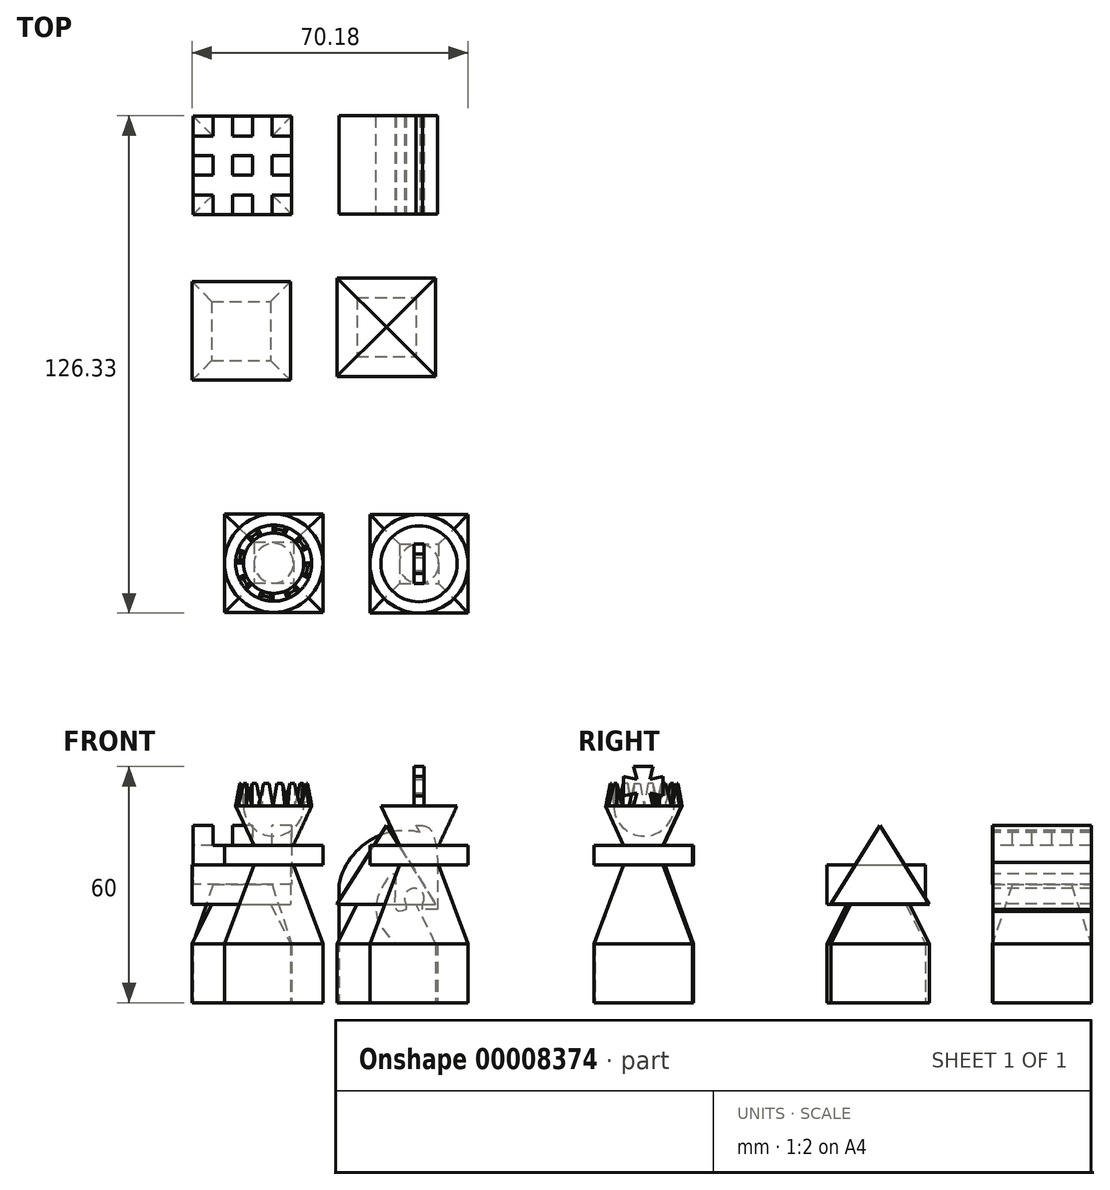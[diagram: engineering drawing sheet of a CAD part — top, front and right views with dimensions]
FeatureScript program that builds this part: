
annotation { "Feature Type Name" : "Feature", "Feature Type Description" : "" }
export const myFeature = defineFeature(function(context is Context, id is Id, definition is map)
    precondition{}
    {
        {
            var Q0;
            Q0=qCreatedBy(makeId("Top.planeOp"),FACE);
            var sketch = newSketch(context, id + "F0", { "sketchPlane" : qUnion([Q0])});
            skLineSegment(sketch, "E0.rect.bottom", {"start": v(-51.31, 37.4) * mm, "end": v(-76.31, 37.4) * mm});
            skLineSegment(sketch, "E0.rect.top", {"start": v(-51.31, 62.4) * mm, "end": v(-76.31, 62.4) * mm});
            skLineSegment(sketch, "E0.rect.left", {"start": v(-51.31, 37.4) * mm, "end": v(-51.31, 62.4) * mm});
            skLineSegment(sketch, "E0.rect.right", {"start": v(-76.31, 37.4) * mm, "end": v(-76.31, 62.4) * mm});
            skPoint(sketch, "E0.rect.middle", {"position": v(-63.81, 49.9) * mm});
            skSolve(sketch);
        }
        {
            var Q0;
            Q0=makeQuery(id+"F0.imprint","IMPRINT",FACE,{"disambiguationData":[TD([[makeQuery(id+"F0.imprint","IMPRINT",EDGE,{"derivedFrom":sQuery(id+"F0.wireOp",EDGE,"E0.rect.bottom")}),-1.0]])]});
            extrude(context, id + "F1", {"entities" : qUnion([Q0]), "depth" : 30 * mm, "hasSecondDirection" : true, "secondDirectionOppositeDirection" : true, "secondDirectionDepth" : 15 * mm});
        }
        {
            var Q0;
            Q0=makeQuery(id+"F1.opExtrude","SWEPT_FACE",FACE,{"disambiguationData":[OSD([sQuery(id+"F0.wireOp",EDGE,"E0.rect.top")])]});
            var sketch = newSketch(context, id + "F2", { "sketchPlane" : qUnion([Q0])});
            skLineSegment(sketch, "E1", {"start": v(51.31, -15) * mm, "end": v(76.31, -15) * mm});
            skLineSegment(sketch, "E2", {"start": v(51.31, 15) * mm, "end": v(56.31, 15) * mm});
            skLineSegment(sketch, "E3", {"start": v(56.31, 15) * mm, "end": v(51.31, 0) * mm});
            skLineSegment(sketch, "E4", {"start": v(76.31, 15) * mm, "end": v(71.31, 15) * mm});
            skLineSegment(sketch, "E5", {"start": v(71.31, 15) * mm, "end": v(76.31, 0) * mm});
            skLineSegment(sketch, "E6", {"start": v(51.31, 15) * mm, "end": v(51.31, 0) * mm});
            skLineSegment(sketch, "E7", {"start": v(76.31, 15) * mm, "end": v(76.31, 0) * mm});
            skSolve(sketch);
        }
        {
            var Q0;
            Q0 = qSketchRegion(id + "F2", true);
            extrude(context, id + "F3", {"entities" : qUnion([Q0]), "operationType" : NewBodyOperationType.REMOVE, "oppositeDirection" : true, "depth" : 25 * mm});
        }
        {
            var Q0;
            {var subQ0=sQuery(id+"F0.wireOp",EDGE,"E0.rect.left");Q0=makeQuery(id+"F3.boolean.opBoolean","SPLIT",FACE,{"disambiguationData":[TD([makeQuery(id+"F3.opExtrude","SWEPT_FACE",FACE,{"disambiguationData":[OSD([sQuery(id+"F2.wireOp",EDGE,"E2")])]})])],"derivedFrom":makeQuery(id+"F1.opExtrude","SWEPT_FACE",FACE,{"disambiguationData":[OSD([subQ0])]})});}
            var sketch = newSketch(context, id + "F4", { "sketchPlane" : qUnion([Q0])});
            skLineSegment(sketch, "E8", {"start": v(37.4, 15) * mm, "end": v(42.4, 15) * mm});
            skLineSegment(sketch, "E9", {"start": v(42.4, 15) * mm, "end": v(37.4, 0) * mm});
            skLineSegment(sketch, "E10", {"start": v(37.4, 0) * mm, "end": v(37.4, 15) * mm});
            skLineSegment(sketch, "E11", {"start": v(62.4, 15) * mm, "end": v(57.4, 15) * mm});
            skLineSegment(sketch, "E12", {"start": v(57.4, 15) * mm, "end": v(62.4, 0) * mm});
            skLineSegment(sketch, "E13", {"start": v(62.4, 0) * mm, "end": v(62.4, 15) * mm});
            skSolve(sketch);
        }
        {
            var Q0;
            Q0=makeQuery(id+"F4.imprint","IMPRINT",FACE,{"disambiguationData":[TD([[makeQuery(id+"F4.imprint","IMPRINT",EDGE,{"derivedFrom":sQuery(id+"F4.wireOp",EDGE,"E8")}),-1.0]])]});
            var Q1;
            Q1=makeQuery(id+"F4.imprint","IMPRINT",FACE,{"disambiguationData":[TD([[makeQuery(id+"F4.imprint","IMPRINT",EDGE,{"derivedFrom":sQuery(id+"F4.wireOp",EDGE,"E11")}),-1.0]])]});
            extrude(context, id + "F5", {"entities" : qUnion([Q0, Q1]), "operationType" : NewBodyOperationType.REMOVE, "oppositeDirection" : true, "depth" : 25 * mm});
        }
        {
            var Q0;
            {var subQ0=sQuery(id+"F0.wireOp",EDGE,"E0.rect.bottom");Q0=makeQuery(id+"F5.boolean.opBoolean","SPLIT",FACE,{"disambiguationData":[TD([makeQuery(id+"F3.boolean.opBoolean","COPY",FACE,{"derivedFrom":makeQuery(id+"F3.opExtrude","SWEPT_FACE",FACE,{"disambiguationData":[OSD([sQuery(id+"F2.wireOp",EDGE,"E2")])]})})])],"derivedFrom":makeQuery(id+"F1.opExtrude","SWEPT_FACE",FACE,{"disambiguationData":[OSD([subQ0])]})});}
            var sketch = newSketch(context, id + "F6", { "sketchPlane" : qUnion([Q0])});
            skLineSegment(sketch, "E14", {"start": v(-71.31, 30) * mm, "end": v(-71.31, 25) * mm});
            skLineSegment(sketch, "E15", {"start": v(-71.31, 25) * mm, "end": v(-66.31, 25) * mm});
            skLineSegment(sketch, "E16", {"start": v(-66.31, 30) * mm, "end": v(-66.31, 25) * mm});
            skLineSegment(sketch, "E17", {"start": v(-61.31, 30) * mm, "end": v(-61.31, 25) * mm});
            skLineSegment(sketch, "E18", {"start": v(-56.31, 30) * mm, "end": v(-56.31, 25) * mm});
            skLineSegment(sketch, "E19.trimOffspring", {"start": v(-61.31, 25) * mm, "end": v(-56.31, 25) * mm});
            skPoint(sketch, "E20.end.orphan", {"position": v(-66.31, 28.3) * mm});
            skPoint(sketch, "E21.start.orphan", {"position": v(-61.31, 28.3) * mm});
            skPoint(sketch, "E22.start.orphan", {"position": v(-56.31, 28.3) * mm});
            skSolve(sketch);
        }
        {
            var Q0;
            {var subQ2=sQuery(id+"F6.wireOp",EDGE,"E14");Q0=makeQuery(id+"F6.imprint","IMPRINT",FACE,{"disambiguationData":[TD([[makeQuery(id+"F6.imprint","IMPRINT",EDGE,{"derivedFrom":subQ2}),1.0]])]});}
            var Q1;
            {var subQ2=sQuery(id+"F6.wireOp",EDGE,"E17");Q1=makeQuery(id+"F6.imprint","IMPRINT",FACE,{"disambiguationData":[TD([[makeQuery(id+"F6.imprint","IMPRINT",EDGE,{"derivedFrom":subQ2}),1.0]])]});}
            extrude(context, id + "F7", {"entities" : qUnion([Q0, Q1]), "operationType" : NewBodyOperationType.REMOVE, "oppositeDirection" : true, "depth" : 25 * mm});
        }
        {
            var Q0;
            {var subQ0=sQuery(id+"F0.wireOp",EDGE,"E0.rect.right");Q0=makeQuery(id+"F3.boolean.opBoolean","SPLIT",FACE,{"disambiguationData":[TD([makeQuery(id+"F3.opExtrude","SWEPT_FACE",FACE,{"disambiguationData":[OSD([sQuery(id+"F2.wireOp",EDGE,"E4")])]})])],"derivedFrom":makeQuery(id+"F1.opExtrude","SWEPT_FACE",FACE,{"disambiguationData":[OSD([subQ0])]})});}
            var sketch = newSketch(context, id + "F8", { "sketchPlane" : qUnion([Q0])});
            skLineSegment(sketch, "E23", {"start": v(-57.4, 25) * mm, "end": v(-52.4, 25) * mm});
            skLineSegment(sketch, "E24", {"start": v(-47.4, 25) * mm, "end": v(-42.4, 25) * mm});
            skLineSegment(sketch, "E25", {"start": v(-57.4, 25) * mm, "end": v(-57.4, 30) * mm});
            skLineSegment(sketch, "E26", {"start": v(-52.4, 25) * mm, "end": v(-52.4, 30) * mm});
            skLineSegment(sketch, "E27", {"start": v(-47.4, 25) * mm, "end": v(-47.4, 30) * mm});
            skLineSegment(sketch, "E28", {"start": v(-42.4, 25) * mm, "end": v(-42.4, 30) * mm});
            skSolve(sketch);
        }
        {
            var Q0;
            Q0=makeQuery(id+"F8.imprint","IMPRINT",FACE,{"disambiguationData":[TD([[makeQuery(id+"F8.imprint","IMPRINT",EDGE,{"derivedFrom":sQuery(id+"F8.wireOp",EDGE,"E23")}),1.0]])]});
            var Q1;
            Q1=makeQuery(id+"F8.imprint","IMPRINT",FACE,{"disambiguationData":[TD([[makeQuery(id+"F8.imprint","IMPRINT",EDGE,{"derivedFrom":sQuery(id+"F8.wireOp",EDGE,"E24")}),1.0]])]});
            extrude(context, id + "F9", {"entities" : qUnion([Q0, Q1]), "operationType" : NewBodyOperationType.REMOVE, "oppositeDirection" : true, "depth" : 25 * mm});
        }
        {
            var Q0;
            Q0=qCreatedBy(makeId("Top.planeOp"),FACE);
            var sketch = newSketch(context, id + "F10", { "sketchPlane" : qUnion([Q0])});
            skLineSegment(sketch, "E29.bottom", {"start": v(-76.64, -4.67) * mm, "end": v(-51.64, -4.67) * mm});
            skLineSegment(sketch, "E29.top", {"start": v(-76.64, 20.33) * mm, "end": v(-51.64, 20.33) * mm});
            skLineSegment(sketch, "E29.left", {"start": v(-76.64, -4.67) * mm, "end": v(-76.64, 20.33) * mm});
            skLineSegment(sketch, "E29.right", {"start": v(-51.64, -4.67) * mm, "end": v(-51.64, 20.33) * mm});
            skSolve(sketch);
        }
        {
            var Q0;
            Q0=makeQuery(id+"F10.imprint","IMPRINT",FACE,{"disambiguationData":[TD([[makeQuery(id+"F10.imprint","IMPRINT",EDGE,{"derivedFrom":sQuery(id+"F10.wireOp",EDGE,"E29.bottom")}),1.0]])]});
            extrude(context, id + "F11", {"entities" : qUnion([Q0]), "depth" : 20 * mm, "hasSecondDirection" : true, "secondDirectionOppositeDirection" : true, "secondDirectionDepth" : 15 * mm});
        }
        {
            var Q0;
            Q0=makeQuery(id+"F11.opExtrude","SWEPT_FACE",FACE,{"disambiguationData":[OSD([sQuery(id+"F10.wireOp",EDGE,"E29.right")])]});
            var sketch = newSketch(context, id + "F12", { "sketchPlane" : qUnion([Q0])});
            skLineSegment(sketch, "E30", {"start": v(-4.67, 0) * mm, "end": v(-4.67, 10) * mm});
            skLineSegment(sketch, "E31", {"start": v(-4.67, 10) * mm, "end": v(0.33, 10) * mm});
            skLineSegment(sketch, "E32", {"start": v(0.33, 10) * mm, "end": v(-4.67, 0) * mm});
            skLineSegment(sketch, "E33", {"start": v(20.33, 10) * mm, "end": v(15.33, 10) * mm});
            skLineSegment(sketch, "E34", {"start": v(15.33, 10) * mm, "end": v(20.33, 0) * mm});
            skLineSegment(sketch, "E35", {"start": v(20.33, 0) * mm, "end": v(20.33, 10) * mm});
            skSolve(sketch);
        }
        {
            var Q0;
            Q0=makeQuery(id+"F12.imprint","IMPRINT",FACE,{"disambiguationData":[TD([[makeQuery(id+"F12.imprint","IMPRINT",EDGE,{"derivedFrom":sQuery(id+"F12.wireOp",EDGE,"E30")}),1.0]])]});
            var Q1;
            Q1=makeQuery(id+"F12.imprint","IMPRINT",FACE,{"disambiguationData":[TD([[makeQuery(id+"F12.imprint","IMPRINT",EDGE,{"derivedFrom":sQuery(id+"F12.wireOp",EDGE,"E33")}),1.0]])]});
            extrude(context, id + "F13", {"entities" : qUnion([Q0, Q1]), "operationType" : NewBodyOperationType.REMOVE, "oppositeDirection" : true, "depth" : 25 * mm});
        }
        {
            var Q0;
            {var subQ0=sQuery(id+"F10.wireOp",EDGE,"E29.bottom");Q0=makeQuery(id+"F13.boolean.opBoolean","SPLIT",FACE,{"disambiguationData":[TD([makeQuery(id+"F13.opExtrude","SWEPT_FACE",FACE,{"disambiguationData":[OSD([sQuery(id+"F12.wireOp",EDGE,"E31")])]})])],"derivedFrom":makeQuery(id+"F11.opExtrude","SWEPT_FACE",FACE,{"disambiguationData":[OSD([subQ0])]})});}
            var sketch = newSketch(context, id + "F14", { "sketchPlane" : qUnion([Q0])});
            skLineSegment(sketch, "E36", {"start": v(-76.64, 0) * mm, "end": v(-76.64, 10) * mm});
            skLineSegment(sketch, "E37", {"start": v(-76.64, 10) * mm, "end": v(-71.64, 10) * mm});
            skLineSegment(sketch, "E38", {"start": v(-71.64, 10) * mm, "end": v(-76.64, 0) * mm});
            skLineSegment(sketch, "E39", {"start": v(-51.64, 10) * mm, "end": v(-56.64, 10) * mm});
            skLineSegment(sketch, "E40", {"start": v(-56.64, 10) * mm, "end": v(-51.64, 0) * mm});
            skLineSegment(sketch, "E41", {"start": v(-51.64, 0) * mm, "end": v(-51.64, 10) * mm});
            skSolve(sketch);
        }
        {
            var Q0;
            Q0=makeQuery(id+"F14.imprint","IMPRINT",FACE,{"disambiguationData":[TD([[makeQuery(id+"F14.imprint","IMPRINT",EDGE,{"derivedFrom":sQuery(id+"F14.wireOp",EDGE,"E36")}),-1.0]])]});
            var Q1;
            Q1=makeQuery(id+"F14.imprint","IMPRINT",FACE,{"disambiguationData":[TD([[makeQuery(id+"F14.imprint","IMPRINT",EDGE,{"derivedFrom":sQuery(id+"F14.wireOp",EDGE,"E39")}),-1.0]])]});
            extrude(context, id + "F15", {"entities" : qUnion([Q0, Q1]), "operationType" : NewBodyOperationType.REMOVE, "oppositeDirection" : true, "depth" : 25 * mm});
        }
        {
            var Q0;
            Q0=qCreatedBy(makeId("Top.planeOp"),FACE);
            var sketch = newSketch(context, id + "F16", { "sketchPlane" : qUnion([Q0])});
            skLineSegment(sketch, "E42.bottom", {"start": v(-39.28, 62.5) * mm, "end": v(-14.28, 62.5) * mm});
            skLineSegment(sketch, "E42.top", {"start": v(-39.28, 37.5) * mm, "end": v(-14.28, 37.5) * mm});
            skLineSegment(sketch, "E42.left", {"start": v(-39.28, 62.5) * mm, "end": v(-39.28, 37.5) * mm});
            skLineSegment(sketch, "E42.right", {"start": v(-14.28, 62.5) * mm, "end": v(-14.28, 37.5) * mm});
            skSolve(sketch);
        }
        {
            var Q0;
            Q0=makeQuery(id+"F16.imprint","IMPRINT",FACE,{"disambiguationData":[TD([[makeQuery(id+"F16.imprint","IMPRINT",EDGE,{"derivedFrom":sQuery(id+"F16.wireOp",EDGE,"E42.bottom")}),-1.0]])]});
            extrude(context, id + "F17", {"entities" : qUnion([Q0]), "depth" : 30 * mm, "hasSecondDirection" : true, "secondDirectionOppositeDirection" : true, "secondDirectionDepth" : 15 * mm});
        }
        {
            var Q0;
            Q0=makeQuery(id+"F17.opExtrude","SWEPT_FACE",FACE,{"disambiguationData":[OSD([sQuery(id+"F16.wireOp",EDGE,"E42.top")])]});
            var sketch = newSketch(context, id + "F18", { "sketchPlane" : qUnion([Q0])});
            skLineSegment(sketch, "E43", {"start": v(-39.28, 0) * mm, "end": v(-39.28, 15) * mm});
            skArc(sketch, "E44", {"start": v(-18.7, 28.27) * mm, "mid": v(-31.8, 26) * mm, "end": v(-39.28, 15) * mm});
            skLineSegment(sketch, "E45", {"start": v(-18.7, 28.27) * mm, "end": v(-19.7, 30) * mm});
            skFitSpline(sketch, "E46", {"points": [v(-19.7, 30) * mm, v(-16.08, 29.03) * mm, v(-14.28, 8.72) * mm], "startDerivative": vector(13.5, 0.62) * mm, "endDerivative": vector(-0.75, -38.03) * mm});
            skLineSegment(sketch, "E47", {"start": v(-14.28, 8.72) * mm, "end": v(-18.1, 8.72) * mm});
            skLineSegment(sketch, "E48", {"start": v(-18.1, 8.72) * mm, "end": v(-18.1, 10.15) * mm});
            skArc(sketch, "E49", {"start": v(-18.1, 10.15) * mm, "mid": v(-20.17, 14.03) * mm, "end": v(-22.23, 10.15) * mm});
            skLineSegment(sketch, "E50", {"start": v(-22.23, 10.15) * mm, "end": v(-22.23, 8.72) * mm});
            skFitSpline(sketch, "E51", {"points": [v(-22.23, 8.72) * mm, v(-24.76, 8.72) * mm, v(-25.18, 17.57) * mm, v(-29.9, 9.99) * mm, v(-25.01, 0) * mm], "startDerivative": vector(-21.5, -9.14) * mm, "endDerivative": vector(26.9, -28.6) * mm});
            skLineSegment(sketch, "E52", {"start": v(-39.28, 0) * mm, "end": v(-14.28, 0) * mm});
            skLineSegment(sketch, "E53", {"start": v(-14.28, 0) * mm, "end": v(-14.28, 30) * mm});
            skLineSegment(sketch, "E54", {"start": v(-14.28, 30) * mm, "end": v(-39.28, 30) * mm});
            skLineSegment(sketch, "E55", {"start": v(-39.28, 30) * mm, "end": v(-39.28, 0) * mm});
            skSolve(sketch);
        }
        {
            var Q0;
            Q0=makeQuery(id+"F18.imprint","IMPRINT",FACE,{"disambiguationData":[TD([[makeQuery(id+"F18.imprint","IMPRINT",EDGE,{"derivedFrom":sQuery(id+"F18.wireOp",EDGE,"E44")}),-1.0]])]});
            var Q1;
            {var subQ0=sQuery(id+"F18.wireOp",EDGE,"E54");var subQ1=sQuery(id+"F18.wireOp",EDGE,"E46");var subQ2=makeQuery(id+"F18.imprint","INTERSECT",VERTEX,{"derivedFrom":[subQ1,subQ0]});Q1=makeQuery(id+"F18.imprint","IMPRINT",FACE,{"disambiguationData":[TD([[makeQuery(id+"F18.imprint","IMPRINT",EDGE,{"disambiguationData":[TD([[subQ2,-1.0]])],"derivedFrom":subQ1}),1.0]])]});}
            var Q2;
            {var subQ0=sQuery(id+"F18.wireOp",EDGE,"E47");Q2=makeQuery(id+"F18.imprint","IMPRINT",FACE,{"disambiguationData":[TD([[makeQuery(id+"F18.imprint","IMPRINT",EDGE,{"derivedFrom":subQ0}),1.0]])]});}
            extrude(context, id + "F19", {"entities" : qUnion([Q0, Q1, Q2]), "operationType" : NewBodyOperationType.REMOVE, "oppositeDirection" : true, "depth" : 25 * mm});
        }
        {
            var Q0;
            Q0=qCreatedBy(makeId("Top.planeOp"),FACE);
            var sketch = newSketch(context, id + "F20", { "sketchPlane" : qUnion([Q0])});
            skLineSegment(sketch, "E56.bottom", {"start": v(-39.73, 21.33) * mm, "end": v(-14.73, 21.33) * mm});
            skLineSegment(sketch, "E56.top", {"start": v(-39.73, -3.67) * mm, "end": v(-14.73, -3.67) * mm});
            skLineSegment(sketch, "E56.left", {"start": v(-39.73, 21.33) * mm, "end": v(-39.73, -3.67) * mm});
            skLineSegment(sketch, "E56.right", {"start": v(-14.73, 21.33) * mm, "end": v(-14.73, -3.67) * mm});
            skSolve(sketch);
        }
        {
            var Q0;
            Q0=makeQuery(id+"F20.imprint","IMPRINT",FACE,{"disambiguationData":[TD([[makeQuery(id+"F20.imprint","IMPRINT",EDGE,{"derivedFrom":sQuery(id+"F20.wireOp",EDGE,"E56.bottom")}),-1.0]])]});
            extrude(context, id + "F21", {"entities" : qUnion([Q0]), "depth" : 30 * mm, "hasSecondDirection" : true, "secondDirectionOppositeDirection" : true, "secondDirectionDepth" : 15 * mm});
        }
        {
            var Q0;
            Q0=makeQuery(id+"F21.opExtrude","SWEPT_FACE",FACE,{"disambiguationData":[OSD([sQuery(id+"F20.wireOp",EDGE,"E56.right")])]});
            var sketch = newSketch(context, id + "F22", { "sketchPlane" : qUnion([Q0])});
            skLineSegment(sketch, "E57", {"start": v(-3.67, 0) * mm, "end": v(-3.67, 10) * mm});
            skLineSegment(sketch, "E58", {"start": v(-3.67, 10) * mm, "end": v(1.33, 10) * mm});
            skLineSegment(sketch, "E59", {"start": v(1.33, 10) * mm, "end": v(-3.67, 0) * mm});
            skLineSegment(sketch, "E60", {"start": v(16.33, 10) * mm, "end": v(21.33, 10) * mm});
            skLineSegment(sketch, "E61", {"start": v(21.33, 10) * mm, "end": v(21.33, 0) * mm});
            skLineSegment(sketch, "E62", {"start": v(21.33, 0) * mm, "end": v(16.33, 10) * mm});
            skSolve(sketch);
        }
        {
            var Q0;
            Q0=makeQuery(id+"F22.imprint","IMPRINT",FACE,{"disambiguationData":[TD([[makeQuery(id+"F22.imprint","IMPRINT",EDGE,{"derivedFrom":sQuery(id+"F22.wireOp",EDGE,"E57")}),1.0]])]});
            var Q1;
            Q1=makeQuery(id+"F22.imprint","IMPRINT",FACE,{"disambiguationData":[TD([[makeQuery(id+"F22.imprint","IMPRINT",EDGE,{"derivedFrom":sQuery(id+"F22.wireOp",EDGE,"E60")}),-1.0]])]});
            extrude(context, id + "F23", {"entities" : qUnion([Q0, Q1]), "operationType" : NewBodyOperationType.REMOVE, "oppositeDirection" : true, "depth" : 25 * mm});
        }
        {
            var Q0;
            {var subQ0=sQuery(id+"F20.wireOp",EDGE,"E56.top");Q0=makeQuery(id+"F23.boolean.opBoolean","SPLIT",FACE,{"disambiguationData":[TD([makeQuery(id+"F23.opExtrude","SWEPT_FACE",FACE,{"disambiguationData":[OSD([sQuery(id+"F22.wireOp",EDGE,"E58")])]})])],"derivedFrom":makeQuery(id+"F21.opExtrude","SWEPT_FACE",FACE,{"disambiguationData":[OSD([subQ0])]})});}
            var sketch = newSketch(context, id + "F24", { "sketchPlane" : qUnion([Q0])});
            skLineSegment(sketch, "E63", {"start": v(-39.73, 10) * mm, "end": v(-39.73, 0) * mm});
            skLineSegment(sketch, "E64", {"start": v(-39.73, 0) * mm, "end": v(-34.73, 10) * mm});
            skLineSegment(sketch, "E65", {"start": v(-34.73, 10) * mm, "end": v(-39.73, 10) * mm});
            skLineSegment(sketch, "E66", {"start": v(-14.73, 10) * mm, "end": v(-19.73, 10) * mm});
            skLineSegment(sketch, "E67", {"start": v(-19.73, 10) * mm, "end": v(-14.73, 0) * mm});
            skLineSegment(sketch, "E68", {"start": v(-14.73, 0) * mm, "end": v(-14.73, 10) * mm});
            skSolve(sketch);
        }
        {
            var Q0;
            Q0=makeQuery(id+"F24.imprint","IMPRINT",FACE,{"disambiguationData":[TD([[makeQuery(id+"F24.imprint","IMPRINT",EDGE,{"derivedFrom":sQuery(id+"F24.wireOp",EDGE,"E63")}),1.0]])]});
            var Q1;
            Q1=makeQuery(id+"F24.imprint","IMPRINT",FACE,{"disambiguationData":[TD([[makeQuery(id+"F24.imprint","IMPRINT",EDGE,{"derivedFrom":sQuery(id+"F24.wireOp",EDGE,"E66")}),-1.0]])]});
            extrude(context, id + "F25", {"entities" : qUnion([Q0, Q1]), "operationType" : NewBodyOperationType.REMOVE, "oppositeDirection" : true, "depth" : 25 * mm});
        }
        {
            var Q0;
            {var subQ0=sQuery(id+"F20.wireOp",EDGE,"E56.right");Q0=makeQuery(id+"F25.boolean.opBoolean","SPLIT",FACE,{"disambiguationData":[TD([makeQuery(id+"F23.boolean.opBoolean","COPY",FACE,{"derivedFrom":makeQuery(id+"F23.opExtrude","SWEPT_FACE",FACE,{"disambiguationData":[OSD([sQuery(id+"F22.wireOp",EDGE,"E58")])]})})])],"derivedFrom":makeQuery(id+"F21.opExtrude","SWEPT_FACE",FACE,{"disambiguationData":[OSD([subQ0])]})});}
            var sketch = newSketch(context, id + "F26", { "sketchPlane" : qUnion([Q0])});
            skLineSegment(sketch, "E69", {"start": v(-3.67, 30) * mm, "end": v(21.33, 30) * mm});
            skLineSegment(sketch, "E70", {"start": v(8.83, 30) * mm, "end": v(-3.67, 10) * mm});
            skLineSegment(sketch, "E71", {"start": v(-3.67, 10) * mm, "end": v(21.33, 10) * mm});
            skLineSegment(sketch, "E72", {"start": v(21.33, 10) * mm, "end": v(8.83, 30) * mm});
            skSolve(sketch);
        }
        {
            var Q0;
            {var subQ3=sQuery(id+"F26.wireOp",EDGE,"E70");Q0=makeQuery(id+"F26.imprint","IMPRINT",FACE,{"disambiguationData":[TD([[makeQuery(id+"F26.imprint","IMPRINT",EDGE,{"derivedFrom":subQ3}),-1.0]])]});}
            var Q1;
            {var subQ3=sQuery(id+"F26.wireOp",EDGE,"E72");Q1=makeQuery(id+"F26.imprint","IMPRINT",FACE,{"disambiguationData":[TD([[makeQuery(id+"F26.imprint","IMPRINT",EDGE,{"derivedFrom":subQ3}),-1.0]])]});}
            extrude(context, id + "F27", {"entities" : qUnion([Q0, Q1]), "operationType" : NewBodyOperationType.REMOVE, "oppositeDirection" : true, "depth" : 25 * mm});
        }
        {
            var Q0;
            {var subQ0=sQuery(id+"F20.wireOp",EDGE,"E56.top");Q0=makeQuery(id+"F23.boolean.opBoolean","SPLIT",FACE,{"disambiguationData":[TD([makeQuery(id+"F23.opExtrude","SWEPT_FACE",FACE,{"disambiguationData":[OSD([sQuery(id+"F22.wireOp",EDGE,"E59")])]})])],"derivedFrom":makeQuery(id+"F21.opExtrude","SWEPT_FACE",FACE,{"disambiguationData":[OSD([subQ0])]})});}
            var sketch = newSketch(context, id + "F28", { "sketchPlane" : qUnion([Q0])});
            skLineSegment(sketch, "E73", {"start": v(-39.73, 30.07) * mm, "end": v(-39.73, 10.07) * mm});
            skLineSegment(sketch, "E74", {"start": v(-39.73, 10.07) * mm, "end": v(-14.73, 10.07) * mm});
            skLineSegment(sketch, "E75", {"start": v(-14.73, 10.07) * mm, "end": v(-14.73, 30.07) * mm});
            skLineSegment(sketch, "E76", {"start": v(-14.73, 30.07) * mm, "end": v(-39.73, 30.07) * mm});
            skLineSegment(sketch, "E77", {"start": v(-39.73, 10.07) * mm, "end": v(-27.23, 30.07) * mm});
            skLineSegment(sketch, "E78", {"start": v(-27.23, 30.07) * mm, "end": v(-14.73, 10.07) * mm});
            skSolve(sketch);
        }
        {
            var Q0;
            {var subQ2=sQuery(id+"F28.wireOp",EDGE,"E73");Q0=makeQuery(id+"F28.imprint","IMPRINT",FACE,{"disambiguationData":[TD([[makeQuery(id+"F28.imprint","IMPRINT",EDGE,{"derivedFrom":subQ2}),1.0]])]});}
            var Q1;
            {var subQ2=sQuery(id+"F28.wireOp",EDGE,"E75");Q1=makeQuery(id+"F28.imprint","IMPRINT",FACE,{"disambiguationData":[TD([[makeQuery(id+"F28.imprint","IMPRINT",EDGE,{"derivedFrom":subQ2}),1.0]])]});}
            extrude(context, id + "F29", {"entities" : qUnion([Q0, Q1]), "operationType" : NewBodyOperationType.REMOVE, "oppositeDirection" : true, "depth" : 25 * mm});
        }
        {
            var Q0;
            Q0=qCreatedBy(makeId("Top.planeOp"),FACE);
            var sketch = newSketch(context, id + "F30", { "sketchPlane" : qUnion([Q0])});
            skLineSegment(sketch, "E79.bottom", {"start": v(-68.4, -38.66) * mm, "end": v(-43.4, -38.66) * mm});
            skLineSegment(sketch, "E79.top", {"start": v(-68.4, -63.66) * mm, "end": v(-43.4, -63.66) * mm});
            skLineSegment(sketch, "E79.left", {"start": v(-68.4, -38.66) * mm, "end": v(-68.4, -63.66) * mm});
            skLineSegment(sketch, "E79.right", {"start": v(-43.4, -38.66) * mm, "end": v(-43.4, -63.66) * mm});
            skSolve(sketch);
        }
        {
            var Q0;
            Q0=makeQuery(id+"F30.imprint","IMPRINT",FACE,{"disambiguationData":[TD([[makeQuery(id+"F30.imprint","IMPRINT",EDGE,{"derivedFrom":sQuery(id+"F30.wireOp",EDGE,"E79.bottom")}),-1.0]])]});
            extrude(context, id + "F31", {"entities" : qUnion([Q0]), "depth" : 25 * mm, "hasSecondDirection" : true, "secondDirectionOppositeDirection" : true, "secondDirectionDepth" : 15 * mm});
        }
        {
            var Q0;
            Q0=makeQuery(id+"F31.opExtrude","SWEPT_FACE",FACE,{"disambiguationData":[OSD([sQuery(id+"F30.wireOp",EDGE,"E79.right")])]});
            var sketch = newSketch(context, id + "F32", { "sketchPlane" : qUnion([Q0])});
            skLineSegment(sketch, "E80", {"start": v(-63.66, 20) * mm, "end": v(-56.16, 20) * mm});
            skLineSegment(sketch, "E81", {"start": v(-56.16, 20) * mm, "end": v(-63.66, 0) * mm});
            skPoint(sketch, "E82.end.orphan", {"position": v(-64.81, 0) * mm});
            skLineSegment(sketch, "E83.trimOffspring", {"start": v(-38.66, 20) * mm, "end": v(-37.97, 20) * mm});
            skLineSegment(sketch, "E84", {"start": v(-45.82, 20) * mm, "end": v(-38.66, 20) * mm});
            skLineSegment(sketch, "E85", {"start": v(-38.66, 0) * mm, "end": v(-45.82, 20) * mm});
            skSolve(sketch);
        }
        {
            var Q0;
            {var subQ2=sQuery(id+"F32.wireOp",EDGE,"E84");Q0=makeQuery(id+"F32.imprint","IMPRINT",FACE,{"disambiguationData":[TD([[makeQuery(id+"F32.imprint","IMPRINT",EDGE,{"derivedFrom":subQ2}),-1.0]])]});}
            var Q1;
            {var subQ2=sQuery(id+"F32.wireOp",EDGE,"E80");Q1=makeQuery(id+"F32.imprint","IMPRINT",FACE,{"disambiguationData":[TD([[makeQuery(id+"F32.imprint","IMPRINT",EDGE,{"derivedFrom":subQ2}),-1.0]])]});}
            extrude(context, id + "F33", {"entities" : qUnion([Q0, Q1]), "operationType" : NewBodyOperationType.REMOVE, "oppositeDirection" : true, "depth" : 25 * mm});
        }
        {
            var Q0;
            Q0=makeQuery(id+"F31.opExtrude","SWEPT_FACE",FACE,{"disambiguationData":[OSD([sQuery(id+"F30.wireOp",EDGE,"E79.top")])]});
            var sketch = newSketch(context, id + "F34", { "sketchPlane" : qUnion([Q0])});
            skLineSegment(sketch, "E86", {"start": v(-68.4, 20) * mm, "end": v(-60.9, 20) * mm});
            skLineSegment(sketch, "E87", {"start": v(-60.9, 20) * mm, "end": v(-68.4, 0) * mm});
            skLineSegment(sketch, "E88", {"start": v(-50.9, 20) * mm, "end": v(-43.4, 0) * mm});
            skPoint(sketch, "E89.end.orphan", {"position": v(-60.9, 17.43) * mm});
            skPoint(sketch, "E90.orphan", {"position": v(-43.4, 17.43) * mm});
            skLineSegment(sketch, "E91.trimOffspring", {"start": v(-50.9, 20) * mm, "end": v(-43.4, 20) * mm});
            skLineSegment(sketch, "E92", {"start": v(-68.4, 20) * mm, "end": v(-68.4, 0) * mm});
            skLineSegment(sketch, "E93", {"start": v(-43.4, 20) * mm, "end": v(-43.4, 0) * mm});
            skSolve(sketch);
        }
        {
            var Q0;
            Q0=makeQuery(id+"F34.imprint","IMPRINT",FACE,{"disambiguationData":[TD([[makeQuery(id+"F34.imprint","IMPRINT",EDGE,{"derivedFrom":sQuery(id+"F34.wireOp",EDGE,"E86")}),-1.0]])]});
            var Q1;
            Q1=makeQuery(id+"F34.imprint","IMPRINT",FACE,{"disambiguationData":[TD([[makeQuery(id+"F34.imprint","IMPRINT",EDGE,{"derivedFrom":sQuery(id+"F34.wireOp",EDGE,"E88")}),1.0]])]});
            extrude(context, id + "F35", {"entities" : qUnion([Q0, Q1]), "operationType" : NewBodyOperationType.REMOVE, "oppositeDirection" : true, "depth" : 25 * mm});
        }
        {
            var Q0;
            Q0=makeQuery(id+"F31.opExtrude","CAP_FACE",FACE,{"disambiguationData":[OSD([sQuery(id+"F30.wireOp",EDGE,"E79.bottom"),sQuery(id+"F30.wireOp",EDGE,"E79.top"),sQuery(id+"F30.wireOp",EDGE,"E79.left"),sQuery(id+"F30.wireOp",EDGE,"E79.right")])],"isStart":false});
            var sketch = newSketch(context, id + "F36", { "sketchPlane" : qUnion([Q0])});
            skLineSegment(sketch, "E94", {"start": v(-68.4, -38.66) * mm, "end": v(-43.4, -63.66) * mm});
            skCircle(sketch, "E95", {"center": v(-55.9, -51.16) * mm, "radius": 12.5 * mm});
            skSolve(sketch);
        }
        {
            var Q0;
            {var subQ0=sQuery(id+"F36.wireOp",EDGE,"E94");var subQ3=sQuery(id+"F36.wireOp",EDGE,"E95");var subQ4=makeQuery(id+"F36.imprint","INTERSECT",VERTEX,{"disambiguationData":[OD(0.0)],"derivedFrom":[subQ0,subQ3]});Q0=makeQuery(id+"F36.imprint","IMPRINT",FACE,{"disambiguationData":[TD([[makeQuery(id+"F36.imprint","IMPRINT",EDGE,{"disambiguationData":[TD([[subQ4,-1.0]])],"derivedFrom":subQ3}),-1.0]])]});}
            var Q1;
            {var subQ0=sQuery(id+"F36.wireOp",EDGE,"E94");var subQ3=sQuery(id+"F36.wireOp",EDGE,"E95");var subQ4=makeQuery(id+"F36.imprint","INTERSECT",VERTEX,{"disambiguationData":[OD(0.0)],"derivedFrom":[subQ0,subQ3]});Q1=makeQuery(id+"F36.imprint","IMPRINT",FACE,{"disambiguationData":[TD([[makeQuery(id+"F36.imprint","IMPRINT",EDGE,{"disambiguationData":[TD([[subQ4,1.0]])],"derivedFrom":subQ3}),-1.0]])]});}
            var Q2;
            {var subQ0=sQuery(id+"F36.wireOp",EDGE,"E95");var subQ1=makeQuery(id+"F31.opExtrude","CAP_EDGE",EDGE,{"disambiguationData":[OSD([sQuery(id+"F30.wireOp",EDGE,"E79.bottom")])],"isStart":false});var subQ2=makeQuery(id+"F36.imprint","INTERSECT",VERTEX,{"derivedFrom":[subQ1,subQ0]});Q2=makeQuery(id+"F36.imprint","IMPRINT",FACE,{"disambiguationData":[TD([[makeQuery(id+"F36.imprint","IMPRINT",EDGE,{"disambiguationData":[TD([[subQ2,1.0]])],"derivedFrom":subQ0}),-1.0]])]});}
            var Q3;
            {var subQ0=sQuery(id+"F36.wireOp",EDGE,"E94");var subQ3=sQuery(id+"F36.wireOp",EDGE,"E95");var subQ4=makeQuery(id+"F36.imprint","INTERSECT",VERTEX,{"disambiguationData":[OD(1.0)],"derivedFrom":[subQ0,subQ3]});Q3=makeQuery(id+"F36.imprint","IMPRINT",FACE,{"disambiguationData":[TD([[makeQuery(id+"F36.imprint","IMPRINT",EDGE,{"disambiguationData":[TD([[subQ4,-1.0]])],"derivedFrom":subQ3}),-1.0]])]});}
            var Q4;
            {var subQ0=sQuery(id+"F36.wireOp",EDGE,"E95");var subQ1=makeQuery(id+"F31.opExtrude","CAP_EDGE",EDGE,{"disambiguationData":[OSD([sQuery(id+"F30.wireOp",EDGE,"E79.left")])],"isStart":false});var subQ2=makeQuery(id+"F36.imprint","INTERSECT",VERTEX,{"derivedFrom":[subQ1,subQ0]});Q4=makeQuery(id+"F36.imprint","IMPRINT",FACE,{"disambiguationData":[TD([[makeQuery(id+"F36.imprint","IMPRINT",EDGE,{"disambiguationData":[TD([[subQ2,-1.0]])],"derivedFrom":subQ0}),-1.0]])]});}
            var Q5;
            {var subQ0=sQuery(id+"F36.wireOp",EDGE,"E94");var subQ3=sQuery(id+"F36.wireOp",EDGE,"E95");var subQ4=makeQuery(id+"F36.imprint","INTERSECT",VERTEX,{"disambiguationData":[OD(1.0)],"derivedFrom":[subQ0,subQ3]});Q5=makeQuery(id+"F36.imprint","IMPRINT",FACE,{"disambiguationData":[TD([[makeQuery(id+"F36.imprint","IMPRINT",EDGE,{"disambiguationData":[TD([[subQ4,1.0]])],"derivedFrom":subQ3}),-1.0]])]});}
            extrude(context, id + "F37", {"entities" : qUnion([Q0, Q1, Q2, Q3, Q4, Q5]), "operationType" : NewBodyOperationType.REMOVE, "oppositeDirection" : true, "depth" : (5) * mm});
        }
        {
            var Q0;
            Q0=qCreatedBy(makeId("Top.planeOp"),FACE);
            var sketch = newSketch(context, id + "F38", { "sketchPlane" : qUnion([Q0])});
            skLineSegment(sketch, "E96.bottom", {"start": v(-31.46, -38.82) * mm, "end": v(-6.46, -38.82) * mm});
            skLineSegment(sketch, "E96.top", {"start": v(-31.46, -63.82) * mm, "end": v(-6.46, -63.82) * mm});
            skLineSegment(sketch, "E96.left", {"start": v(-31.46, -38.82) * mm, "end": v(-31.46, -63.82) * mm});
            skLineSegment(sketch, "E96.right", {"start": v(-6.46, -38.82) * mm, "end": v(-6.46, -63.82) * mm});
            skSolve(sketch);
        }
        {
            var Q0;
            Q0=makeQuery(id+"F38.imprint","IMPRINT",FACE,{"disambiguationData":[TD([[makeQuery(id+"F38.imprint","IMPRINT",EDGE,{"derivedFrom":sQuery(id+"F38.wireOp",EDGE,"E96.bottom")}),-1.0]])]});
            extrude(context, id + "F39", {"entities" : qUnion([Q0]), "depth" : 25 * mm, "hasSecondDirection" : true, "secondDirectionOppositeDirection" : true, "secondDirectionDepth" : 15 * mm});
        }
        {
            var Q0;
            Q0=makeQuery(id+"F39.opExtrude","SWEPT_FACE",FACE,{"disambiguationData":[OSD([sQuery(id+"F38.wireOp",EDGE,"E96.right")])]});
            var sketch = newSketch(context, id + "F40", { "sketchPlane" : qUnion([Q0])});
            skLineSegment(sketch, "E97", {"start": v(-63.82, 25) * mm, "end": v(-63.82, 0) * mm});
            skLineSegment(sketch, "E98", {"start": v(-63.82, 0) * mm, "end": v(-38.82, 0) * mm});
            skLineSegment(sketch, "E99", {"start": v(-38.82, 0) * mm, "end": v(-38.82, 25) * mm});
            skLineSegment(sketch, "E100", {"start": v(-38.82, 25) * mm, "end": v(-63.82, 25) * mm});
            skLineSegment(sketch, "E101", {"start": v(-63.82, 0) * mm, "end": v(-63.82, 20) * mm});
            skLineSegment(sketch, "E102", {"start": v(-63.82, 20) * mm, "end": v(-56.32, 20) * mm});
            skLineSegment(sketch, "E103", {"start": v(-56.32, 20) * mm, "end": v(-63.82, 0) * mm});
            skLineSegment(sketch, "E104", {"start": v(-38.82, 0) * mm, "end": v(-38.82, 20) * mm});
            skLineSegment(sketch, "E105", {"start": v(-38.82, 20) * mm, "end": v(-46.32, 20) * mm});
            skLineSegment(sketch, "E106", {"start": v(-46.32, 20) * mm, "end": v(-38.82, 0) * mm});
            skLineSegment(sketch, "E107", {"start": v(-38.82, 20) * mm, "end": v(-38.82, 0) * mm});
            skSolve(sketch);
        }
        {
            var Q0;
            {var subQ2=sQuery(id+"F40.wireOp",EDGE,"E102");Q0=makeQuery(id+"F40.imprint","IMPRINT",FACE,{"disambiguationData":[TD([[makeQuery(id+"F40.imprint","IMPRINT",EDGE,{"derivedFrom":subQ2}),-1.0]])]});}
            var Q1;
            {var subQ2=sQuery(id+"F40.wireOp",EDGE,"E105");Q1=makeQuery(id+"F40.imprint","IMPRINT",FACE,{"disambiguationData":[TD([[makeQuery(id+"F40.imprint","IMPRINT",EDGE,{"derivedFrom":subQ2}),1.0]])]});}
            extrude(context, id + "F41", {"entities" : qUnion([Q0, Q1]), "operationType" : NewBodyOperationType.REMOVE, "oppositeDirection" : true, "depth" : 25 * mm});
        }
        {
            var Q0;
            {var subQ2=sQuery(id+"F38.wireOp",EDGE,"E96.top");Q0=makeQuery(id+"F41.boolean.opBoolean","SPLIT",FACE,{"disambiguationData":[TD([makeQuery(id+"F41.opExtrude","SWEPT_FACE",FACE,{"disambiguationData":[OSD([sQuery(id+"F40.wireOp",EDGE,"E103")])]})])],"derivedFrom":makeQuery(id+"F39.opExtrude","SWEPT_FACE",FACE,{"disambiguationData":[OSD([subQ2])]})});}
            var sketch = newSketch(context, id + "F42", { "sketchPlane" : qUnion([Q0])});
            skLineSegment(sketch, "E108", {"start": v(-31.46, 0) * mm, "end": v(-31.46, 20) * mm});
            skLineSegment(sketch, "E109", {"start": v(-31.46, 20) * mm, "end": v(-23.96, 20) * mm});
            skLineSegment(sketch, "E110", {"start": v(-23.96, 20) * mm, "end": v(-31.46, 0) * mm});
            skLineSegment(sketch, "E111", {"start": v(-6.46, 0) * mm, "end": v(-6.46, 20) * mm});
            skLineSegment(sketch, "E112", {"start": v(-6.46, 20) * mm, "end": v(-13.96, 20) * mm});
            skLineSegment(sketch, "E113", {"start": v(-13.96, 20) * mm, "end": v(-6.46, 0) * mm});
            skLineSegment(sketch, "E114.bottom", {"start": v(-31.46, 20) * mm, "end": v(-6.46, 20) * mm});
            skLineSegment(sketch, "E114.top", {"start": v(-31.46, 0) * mm, "end": v(-6.46, 0) * mm});
            skLineSegment(sketch, "E114.left", {"start": v(-31.46, 20) * mm, "end": v(-31.46, 0) * mm});
            skLineSegment(sketch, "E114.right", {"start": v(-6.46, 20) * mm, "end": v(-6.46, 0) * mm});
            skSolve(sketch);
        }
        {
            var Q0;
            Q0=makeQuery(id+"F42.imprint","IMPRINT",FACE,{"disambiguationData":[TD([[makeQuery(id+"F42.imprint","IMPRINT",EDGE,{"derivedFrom":sQuery(id+"F42.wireOp",EDGE,"E108")}),-1.0]])]});
            var Q1;
            Q1=makeQuery(id+"F42.imprint","IMPRINT",FACE,{"disambiguationData":[TD([[makeQuery(id+"F42.imprint","IMPRINT",EDGE,{"derivedFrom":sQuery(id+"F42.wireOp",EDGE,"E111")}),1.0]])]});
            extrude(context, id + "F43", {"entities" : qUnion([Q0, Q1]), "operationType" : NewBodyOperationType.REMOVE, "oppositeDirection" : true, "depth" : 25 * mm});
        }
        {
            var Q0;
            Q0=makeQuery(id+"F39.opExtrude","CAP_FACE",FACE,{"disambiguationData":[OSD([sQuery(id+"F38.wireOp",EDGE,"E96.bottom"),sQuery(id+"F38.wireOp",EDGE,"E96.top"),sQuery(id+"F38.wireOp",EDGE,"E96.left"),sQuery(id+"F38.wireOp",EDGE,"E96.right")])],"isStart":false});
            var sketch = newSketch(context, id + "F44", { "sketchPlane" : qUnion([Q0])});
            skLineSegment(sketch, "E115", {"start": v(-31.46, -38.82) * mm, "end": v(-6.46, -63.82) * mm});
            skCircle(sketch, "E116", {"center": v(-18.96, -51.32) * mm, "radius": 12.5 * mm});
            skSolve(sketch);
        }
        {
            var Q0;
            {var subQ0=sQuery(id+"F44.wireOp",EDGE,"E115");var subQ3=sQuery(id+"F44.wireOp",EDGE,"E116");var subQ4=makeQuery(id+"F44.imprint","INTERSECT",VERTEX,{"disambiguationData":[OD(0.0)],"derivedFrom":[subQ0,subQ3]});Q0=makeQuery(id+"F44.imprint","IMPRINT",FACE,{"disambiguationData":[TD([[makeQuery(id+"F44.imprint","IMPRINT",EDGE,{"disambiguationData":[TD([[subQ4,-1.0]])],"derivedFrom":subQ3}),-1.0]])]});}
            var Q1;
            {var subQ0=sQuery(id+"F44.wireOp",EDGE,"E115");var subQ3=sQuery(id+"F44.wireOp",EDGE,"E116");var subQ4=makeQuery(id+"F44.imprint","INTERSECT",VERTEX,{"disambiguationData":[OD(0.0)],"derivedFrom":[subQ0,subQ3]});Q1=makeQuery(id+"F44.imprint","IMPRINT",FACE,{"disambiguationData":[TD([[makeQuery(id+"F44.imprint","IMPRINT",EDGE,{"disambiguationData":[TD([[subQ4,1.0]])],"derivedFrom":subQ3}),-1.0]])]});}
            var Q2;
            {var subQ0=sQuery(id+"F44.wireOp",EDGE,"E116");var subQ1=makeQuery(id+"F39.opExtrude","CAP_EDGE",EDGE,{"disambiguationData":[OSD([sQuery(id+"F38.wireOp",EDGE,"E96.bottom")])],"isStart":false});var subQ2=makeQuery(id+"F44.imprint","INTERSECT",VERTEX,{"derivedFrom":[subQ1,subQ0]});Q2=makeQuery(id+"F44.imprint","IMPRINT",FACE,{"disambiguationData":[TD([[makeQuery(id+"F44.imprint","IMPRINT",EDGE,{"disambiguationData":[TD([[subQ2,1.0]])],"derivedFrom":subQ0}),-1.0]])]});}
            var Q3;
            {var subQ0=sQuery(id+"F44.wireOp",EDGE,"E115");var subQ3=sQuery(id+"F44.wireOp",EDGE,"E116");var subQ4=makeQuery(id+"F44.imprint","INTERSECT",VERTEX,{"disambiguationData":[OD(1.0)],"derivedFrom":[subQ0,subQ3]});Q3=makeQuery(id+"F44.imprint","IMPRINT",FACE,{"disambiguationData":[TD([[makeQuery(id+"F44.imprint","IMPRINT",EDGE,{"disambiguationData":[TD([[subQ4,-1.0]])],"derivedFrom":subQ3}),-1.0]])]});}
            var Q4;
            {var subQ0=sQuery(id+"F44.wireOp",EDGE,"E115");var subQ3=sQuery(id+"F44.wireOp",EDGE,"E116");var subQ4=makeQuery(id+"F44.imprint","INTERSECT",VERTEX,{"disambiguationData":[OD(1.0)],"derivedFrom":[subQ0,subQ3]});Q4=makeQuery(id+"F44.imprint","IMPRINT",FACE,{"disambiguationData":[TD([[makeQuery(id+"F44.imprint","IMPRINT",EDGE,{"disambiguationData":[TD([[subQ4,1.0]])],"derivedFrom":subQ3}),-1.0]])]});}
            var Q5;
            {var subQ0=sQuery(id+"F44.wireOp",EDGE,"E116");var subQ1=makeQuery(id+"F39.opExtrude","CAP_EDGE",EDGE,{"disambiguationData":[OSD([sQuery(id+"F38.wireOp",EDGE,"E96.left")])],"isStart":false});var subQ2=makeQuery(id+"F44.imprint","INTERSECT",VERTEX,{"derivedFrom":[subQ1,subQ0]});Q5=makeQuery(id+"F44.imprint","IMPRINT",FACE,{"disambiguationData":[TD([[makeQuery(id+"F44.imprint","IMPRINT",EDGE,{"disambiguationData":[TD([[subQ2,-1.0]])],"derivedFrom":subQ0}),-1.0]])]});}
            extrude(context, id + "F45", {"entities" : qUnion([Q0, Q1, Q2, Q3, Q4, Q5]), "operationType" : NewBodyOperationType.REMOVE, "oppositeDirection" : true, "depth" : 5 * mm});
        }
        {
            var Q0;
            Q0=makeQuery(id+"F39.opExtrude","CAP_FACE",FACE,{"disambiguationData":[OSD([sQuery(id+"F38.wireOp",EDGE,"E96.bottom"),sQuery(id+"F38.wireOp",EDGE,"E96.top"),sQuery(id+"F38.wireOp",EDGE,"E96.left"),sQuery(id+"F38.wireOp",EDGE,"E96.right")])],"isStart":false});
            var sketch = newSketch(context, id + "F46", { "sketchPlane" : qUnion([Q0])});
            skCircle(sketch, "E117", {"center": v(-18.96, -51.32) * mm, "radius": 5 * mm});
            skSolve(sketch);
        }
        {
            var Q0;
            Q0=makeQuery(id+"F46.imprint","IMPRINT",FACE,{"disambiguationData":[TD([[makeQuery(id+"F46.imprint","IMPRINT",EDGE,{"derivedFrom":sQuery(id+"F46.wireOp",EDGE,"E117")}),1.0]])]});
            extrude(context, id + "F47", {"entities" : qUnion([Q0]), "operationType" : NewBodyOperationType.ADD, "depth" : 10 * mm, "hasDraft" : true, "draftAngle" : 25 * degree});
        }
        {
            var Q0;
            Q0=makeQuery(id+"F47.opExtrude","CAP_FACE",FACE,{"disambiguationData":[OSD([sQuery(id+"F46.wireOp",EDGE,"E117")])],"isStart":false});
            var sketch = newSketch(context, id + "F48", { "sketchPlane" : qUnion([Q0])});
            skLineSegment(sketch, "E118.bottom", {"start": v(-17.7, -56.32) * mm, "end": v(-20.2, -56.32) * mm});
            skLineSegment(sketch, "E118.top", {"start": v(-17.7, -46.32) * mm, "end": v(-20.2, -46.32) * mm});
            skLineSegment(sketch, "E118.left", {"start": v(-17.7, -56.32) * mm, "end": v(-17.7, -46.32) * mm});
            skLineSegment(sketch, "E118.right", {"start": v(-20.2, -56.32) * mm, "end": v(-20.2, -46.32) * mm});
            skPoint(sketch, "E118.middle", {"position": v(-18.96, -51.32) * mm});
            skSolve(sketch);
        }
        {
            var Q0;
            Q0=makeQuery(id+"F48.imprint","IMPRINT",FACE,{"disambiguationData":[TD([[makeQuery(id+"F48.imprint","IMPRINT",EDGE,{"derivedFrom":sQuery(id+"F48.wireOp",EDGE,"E118.bottom")}),-1.0]])]});
            extrude(context, id + "F49", {"entities" : qUnion([Q0]), "operationType" : NewBodyOperationType.ADD, "depth" : 10 * mm});
        }
        {
            var Q0;
            Q0=makeQuery(id+"F31.opExtrude","CAP_FACE",FACE,{"disambiguationData":[OSD([sQuery(id+"F30.wireOp",EDGE,"E79.bottom"),sQuery(id+"F30.wireOp",EDGE,"E79.top"),sQuery(id+"F30.wireOp",EDGE,"E79.left"),sQuery(id+"F30.wireOp",EDGE,"E79.right")])],"isStart":false});
            var sketch = newSketch(context, id + "F50", { "sketchPlane" : qUnion([Q0])});
            skCircle(sketch, "E119", {"center": v(-55.9, -51.16) * mm, "radius": 5 * mm});
            skSolve(sketch);
        }
        {
            var Q0;
            Q0=makeQuery(id+"F50.imprint","IMPRINT",FACE,{"disambiguationData":[TD([[makeQuery(id+"F50.imprint","IMPRINT",EDGE,{"derivedFrom":sQuery(id+"F50.wireOp",EDGE,"E119")}),1.0]])]});
            extrude(context, id + "F51", {"entities" : qUnion([Q0]), "operationType" : NewBodyOperationType.ADD, "depth" : 10 * mm, "hasDraft" : true, "draftAngle" : 25 * degree});
        }
        {
            var Q0;
            Q0=makeQuery(id+"F51.opExtrude","CAP_FACE",FACE,{"disambiguationData":[OSD([sQuery(id+"F50.wireOp",EDGE,"E119")])],"isStart":false});
            var sketch = newSketch(context, id + "F52", { "sketchPlane" : qUnion([Q0])});
            skArc(sketch, "E120", {"start": v(-63.55, -51.16) * mm, "mid": v(-55.9, -58.82) * mm, "end": v(-48.23, -51.16) * mm});
            skLineSegment(sketch, "E121", {"start": v(-65.55, -51.16) * mm, "end": v(-46.23, -51.16) * mm});
            skSolve(sketch);
        }
        {
            var Q0;
            {var subQ0=sQuery(id+"F52.wireOp",EDGE,"E120");Q0=makeQuery(id+"F52.imprint","IMPRINT",FACE,{"disambiguationData":[TD([[makeQuery(id+"F52.imprint","IMPRINT",EDGE,{"derivedFrom":subQ0}),1.0]])]});}
            var Q1;
            Q1=sQuery(id+"F52.wireOp",EDGE,"E121");
            revolve(context, id + "F53", {"operationType" : NewBodyOperationType.REMOVE, "entities" : qUnion([Q0]), "axis" : qUnion([Q1]), "revolveType" : RevolveType.ONE_DIRECTION, "angle" : 180 * degree});
        }
        {
            var Q0;
            Q0=makeQuery(id+"F51.opExtrude","CAP_FACE",FACE,{"disambiguationData":[OSD([sQuery(id+"F50.wireOp",EDGE,"E119")])],"isStart":false});
            var sketch = newSketch(context, id + "F54", { "sketchPlane" : qUnion([Q0])});
            skLineSegment(sketch, "E122", {"start": v(-56.06, -43.5) * mm, "end": v(-56.06, -58.82) * mm});
            skLineSegment(sketch, "E123", {"start": v(-63.55, -51.16) * mm, "end": v(-48.23, -51.16) * mm});
            skPoint(sketch, "E123.startSnap0", {"position": v(-56.06, -51.16) * mm});
            skLineSegment(sketch, "E124", {"start": v(-50.56, -45.66) * mm, "end": v(-56.06, -51.16) * mm});
            skLineSegment(sketch, "E125", {"start": v(-50.56, -45.66) * mm, "end": v(-61.4, -56.5) * mm});
            skLineSegment(sketch, "E126", {"start": v(-61.4, -45.83) * mm, "end": v(-56.06, -51.16) * mm});
            skLineSegment(sketch, "E127", {"start": v(-61.4, -45.83) * mm, "end": v(-50.56, -56.66) * mm});
            skLineSegment(sketch, "E128", {"start": v(-65.55, -51.16) * mm, "end": v(-63.55, -51.16) * mm});
            skLineSegment(sketch, "E129", {"start": v(-48.23, -51.16) * mm, "end": v(-46.23, -51.16) * mm});
            skLineSegment(sketch, "E130", {"start": v(-56.06, -43.5) * mm, "end": v(-56.06, -60.82) * mm});
            skLineSegment(sketch, "E131", {"start": v(-56.06, -58.82) * mm, "end": v(-56.06, -41.5) * mm});
            skLineSegment(sketch, "E132", {"start": v(-61.4, -45.83) * mm, "end": v(-62.83, -44.44) * mm});
            skLineSegment(sketch, "E133", {"start": v(-50.56, -45.66) * mm, "end": v(-49.17, -44.22) * mm});
            skLineSegment(sketch, "E134", {"start": v(-50.56, -56.66) * mm, "end": v(-49.17, -58.1) * mm});
            skLineSegment(sketch, "E135", {"start": v(-61.4, -56.5) * mm, "end": v(-62.84, -57.88) * mm});
            skLineSegment(sketch, "E136", {"start": v(-63.02, -53.98) * mm, "end": v(-48.86, -48.11) * mm});
            skLineSegment(sketch, "E137", {"start": v(-63.02, -48.34) * mm, "end": v(-48.86, -54.2) * mm});
            skLineSegment(sketch, "E138", {"start": v(-53.07, -58.29) * mm, "end": v(-58.94, -44.13) * mm});
            skLineSegment(sketch, "E139", {"start": v(-58.94, -58.2) * mm, "end": v(-53.07, -44.03) * mm});
            skLineSegment(sketch, "E140", {"start": v(-63.02, -48.34) * mm, "end": v(-64.88, -47.62) * mm});
            skLineSegment(sketch, "E141", {"start": v(-58.94, -44.13) * mm, "end": v(-59.83, -42.34) * mm});
            skLineSegment(sketch, "E142", {"start": v(-53.07, -44.03) * mm, "end": v(-52.24, -42.21) * mm});
            skLineSegment(sketch, "E143", {"start": v(-48.86, -48.11) * mm, "end": v(-47.02, -47.33) * mm});
            skLineSegment(sketch, "E144", {"start": v(-53.07, -58.29) * mm, "end": v(-52.31, -60.14) * mm});
            skLineSegment(sketch, "E145", {"start": v(-48.86, -54.2) * mm, "end": v(-47.01, -54.97) * mm});
            skLineSegment(sketch, "E146", {"start": v(-63.02, -53.98) * mm, "end": v(-64.85, -54.8) * mm});
            skLineSegment(sketch, "E147", {"start": v(-58.94, -58.2) * mm, "end": v(-59.75, -60.02) * mm});
            skSolve(sketch);
        }
        {
            var Q0;
            {var subQ5=sQuery(id+"F54.wireOp",EDGE,"E142");Q0=makeQuery(id+"F54.imprint","IMPRINT",FACE,{"disambiguationData":[TD([[makeQuery(id+"F54.imprint","IMPRINT",EDGE,{"derivedFrom":subQ5}),1.0]])]});}
            var Q1;
            {var subQ0=sQuery(id+"F54.wireOp",EDGE,"E133");Q1=makeQuery(id+"F54.imprint","IMPRINT",FACE,{"disambiguationData":[TD([[makeQuery(id+"F54.imprint","IMPRINT",EDGE,{"derivedFrom":subQ0}),-1.0]])]});}
            var Q2;
            {var subQ0=sQuery(id+"F54.wireOp",EDGE,"E129");Q2=makeQuery(id+"F54.imprint","IMPRINT",FACE,{"disambiguationData":[TD([[makeQuery(id+"F54.imprint","IMPRINT",EDGE,{"derivedFrom":subQ0}),-1.0]])]});}
            var Q3;
            {var subQ0=sQuery(id+"F54.wireOp",EDGE,"E134");Q3=makeQuery(id+"F54.imprint","IMPRINT",FACE,{"disambiguationData":[TD([[makeQuery(id+"F54.imprint","IMPRINT",EDGE,{"derivedFrom":subQ0}),-1.0]])]});}
            var Q4;
            {var subQ0=sQuery(id+"F54.wireOp",EDGE,"E130");Q4=makeQuery(id+"F54.imprint","IMPRINT",FACE,{"disambiguationData":[TD([[makeQuery(id+"F54.imprint","IMPRINT",EDGE,{"derivedFrom":subQ0}),-1.0]])]});}
            var Q5;
            {var subQ0=sQuery(id+"F54.wireOp",EDGE,"E135");Q5=makeQuery(id+"F54.imprint","IMPRINT",FACE,{"disambiguationData":[TD([[makeQuery(id+"F54.imprint","IMPRINT",EDGE,{"derivedFrom":subQ0}),-1.0]])]});}
            var Q6;
            {var subQ0=sQuery(id+"F54.wireOp",EDGE,"E128");Q6=makeQuery(id+"F54.imprint","IMPRINT",FACE,{"disambiguationData":[TD([[makeQuery(id+"F54.imprint","IMPRINT",EDGE,{"derivedFrom":subQ0}),1.0]])]});}
            var Q7;
            {var subQ0=sQuery(id+"F54.wireOp",EDGE,"E132");Q7=makeQuery(id+"F54.imprint","IMPRINT",FACE,{"disambiguationData":[TD([[makeQuery(id+"F54.imprint","IMPRINT",EDGE,{"derivedFrom":subQ0}),-1.0]])]});}
            extrude(context, id + "F55", {"entities" : qUnion([Q0, Q1, Q2, Q3, Q4, Q5, Q6, Q7]), "operationType" : NewBodyOperationType.ADD, "depth" : 10 * mm, "hasDraft" : true, "draftAngle" : 10 * degree, "draftPullDirection" : true});
        }
        {
            var Q0;
            Q0=makeQuery(id+"F49.opExtrude","SWEPT_FACE",FACE,{"disambiguationData":[OSD([sQuery(id+"F48.wireOp",EDGE,"E118.left")])]});
            var sketch = newSketch(context, id + "F56", { "sketchPlane" : qUnion([Q0])});
            skLineSegment(sketch, "E148", {"start": v(-56.32, 45) * mm, "end": v(-46.32, 35) * mm});
            skLineSegment(sketch, "E149", {"start": v(-56.32, 35) * mm, "end": v(-46.32, 45) * mm});
            skLineSegment(sketch, "E150", {"start": v(-56.32, 45) * mm, "end": v(-51.32, 45) * mm});
            skLineSegment(sketch, "E151", {"start": v(-51.32, 45) * mm, "end": v(-46.32, 45) * mm});
            skLineSegment(sketch, "E152", {"start": v(-46.32, 45) * mm, "end": v(-46.32, 40) * mm});
            skLineSegment(sketch, "E153", {"start": v(-46.32, 40) * mm, "end": v(-46.32, 35) * mm});
            skLineSegment(sketch, "E154", {"start": v(-46.32, 35) * mm, "end": v(-51.32, 35) * mm});
            skLineSegment(sketch, "E155", {"start": v(-51.32, 35) * mm, "end": v(-56.32, 35) * mm});
            skLineSegment(sketch, "E156", {"start": v(-56.32, 35) * mm, "end": v(-56.32, 40) * mm});
            skLineSegment(sketch, "E157", {"start": v(-56.32, 40) * mm, "end": v(-56.32, 45) * mm});
            skLineSegment(sketch, "E158", {"start": v(-51.32, 45) * mm, "end": v(-53.82, 35) * mm});
            skLineSegment(sketch, "E159", {"start": v(-48.82, 35) * mm, "end": v(-51.32, 45) * mm});
            skLineSegment(sketch, "E160", {"start": v(-46.32, 40) * mm, "end": v(-56.32, 42.5) * mm});
            skLineSegment(sketch, "E161", {"start": v(-46.32, 40) * mm, "end": v(-56.32, 37.5) * mm});
            skLineSegment(sketch, "E162", {"start": v(-51.32, 35) * mm, "end": v(-48.82, 45) * mm});
            skLineSegment(sketch, "E163", {"start": v(-51.32, 35) * mm, "end": v(-53.82, 45) * mm});
            skLineSegment(sketch, "E164", {"start": v(-56.32, 40) * mm, "end": v(-46.32, 42.5) * mm});
            skLineSegment(sketch, "E165", {"start": v(-56.32, 40) * mm, "end": v(-46.32, 37.5) * mm});
            skSolve(sketch);
        }
        {
            var Q0;
            {var subQ0=sQuery(id+"F56.wireOp",EDGE,"E155");var subQ3=sQuery(id+"F56.wireOp",EDGE,"E158");var subQ5=makeQuery(id+"F56.imprint","INTERSECT",VERTEX,{"derivedFrom":[subQ0,subQ3]});Q0=makeQuery(id+"F56.imprint","IMPRINT",FACE,{"disambiguationData":[TD([[makeQuery(id+"F56.imprint","IMPRINT",EDGE,{"disambiguationData":[TD([[subQ5,1.0]])],"derivedFrom":subQ0}),1.0]])]});}
            var Q1;
            {var subQ0=sQuery(id+"F56.wireOp",EDGE,"E156");var subQ3=sQuery(id+"F56.wireOp",EDGE,"E161");var subQ5=makeQuery(id+"F56.imprint","INTERSECT",VERTEX,{"derivedFrom":[subQ0,subQ3]});Q1=makeQuery(id+"F56.imprint","IMPRINT",FACE,{"disambiguationData":[TD([[makeQuery(id+"F56.imprint","IMPRINT",EDGE,{"disambiguationData":[TD([[subQ5,-1.0]])],"derivedFrom":subQ0}),1.0]])]});}
            var Q2;
            {var subQ0=sQuery(id+"F56.wireOp",EDGE,"E154");var subQ3=sQuery(id+"F56.wireOp",EDGE,"E159");var subQ5=makeQuery(id+"F56.imprint","INTERSECT",VERTEX,{"derivedFrom":[subQ0,subQ3]});Q2=makeQuery(id+"F56.imprint","IMPRINT",FACE,{"disambiguationData":[TD([[makeQuery(id+"F56.imprint","IMPRINT",EDGE,{"disambiguationData":[TD([[subQ5,-1.0]])],"derivedFrom":subQ0}),1.0]])]});}
            var Q3;
            {var subQ0=sQuery(id+"F56.wireOp",EDGE,"E153");var subQ3=sQuery(id+"F56.wireOp",EDGE,"E165");var subQ5=makeQuery(id+"F56.imprint","INTERSECT",VERTEX,{"derivedFrom":[subQ0,subQ3]});Q3=makeQuery(id+"F56.imprint","IMPRINT",FACE,{"disambiguationData":[TD([[makeQuery(id+"F56.imprint","IMPRINT",EDGE,{"disambiguationData":[TD([[subQ5,-1.0]])],"derivedFrom":subQ0}),-1.0]])]});}
            var Q4;
            {var subQ0=sQuery(id+"F56.wireOp",EDGE,"E152");var subQ3=sQuery(id+"F56.wireOp",EDGE,"E164");var subQ5=makeQuery(id+"F56.imprint","INTERSECT",VERTEX,{"derivedFrom":[subQ0,subQ3]});Q4=makeQuery(id+"F56.imprint","IMPRINT",FACE,{"disambiguationData":[TD([[makeQuery(id+"F56.imprint","IMPRINT",EDGE,{"disambiguationData":[TD([[subQ5,1.0]])],"derivedFrom":subQ0}),-1.0]])]});}
            var Q5;
            {var subQ0=sQuery(id+"F56.wireOp",EDGE,"E151");var subQ3=sQuery(id+"F56.wireOp",EDGE,"E162");var subQ5=makeQuery(id+"F56.imprint","INTERSECT",VERTEX,{"derivedFrom":[subQ0,subQ3]});Q5=makeQuery(id+"F56.imprint","IMPRINT",FACE,{"disambiguationData":[TD([[makeQuery(id+"F56.imprint","IMPRINT",EDGE,{"disambiguationData":[TD([[subQ5,-1.0]])],"derivedFrom":subQ0}),-1.0]])]});}
            var Q6;
            {var subQ0=sQuery(id+"F56.wireOp",EDGE,"E150");var subQ3=sQuery(id+"F56.wireOp",EDGE,"E163");var subQ5=makeQuery(id+"F56.imprint","INTERSECT",VERTEX,{"derivedFrom":[subQ0,subQ3]});Q6=makeQuery(id+"F56.imprint","IMPRINT",FACE,{"disambiguationData":[TD([[makeQuery(id+"F56.imprint","IMPRINT",EDGE,{"disambiguationData":[TD([[subQ5,1.0]])],"derivedFrom":subQ0}),-1.0]])]});}
            var Q7;
            {var subQ0=sQuery(id+"F56.wireOp",EDGE,"E157");var subQ3=sQuery(id+"F56.wireOp",EDGE,"E160");var subQ5=makeQuery(id+"F56.imprint","INTERSECT",VERTEX,{"derivedFrom":[subQ0,subQ3]});Q7=makeQuery(id+"F56.imprint","IMPRINT",FACE,{"disambiguationData":[TD([[makeQuery(id+"F56.imprint","IMPRINT",EDGE,{"disambiguationData":[TD([[subQ5,1.0]])],"derivedFrom":subQ0}),1.0]])]});}
            extrude(context, id + "F57", {"entities" : qUnion([Q0, Q1, Q2, Q3, Q4, Q5, Q6, Q7]), "operationType" : NewBodyOperationType.REMOVE, "oppositeDirection" : true, "depth" : 25 * mm, "offsetDistance" : 25 * mm});
        }
    });
